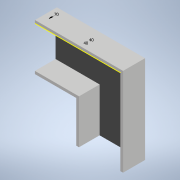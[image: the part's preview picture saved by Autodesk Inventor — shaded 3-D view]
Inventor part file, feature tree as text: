
AUTODESK INVENTOR PART (.ipt)
format: ipt  version: 2022 (Build 260153000, 153)  size: 157,696 bytes
history: native  units: mm
features: sketch x3, extrude x2, projected_geometry x2, other x1
ambient origin geometry x8: Origin, YZ Plane, XZ Plane, XY Plane, X Axis, Y Axis, Z Axis, Center Point
bodies: Body1 (feature_tree)
feature tree (8):
  other  "Твердое тело1"
  extrude  "Выдавливание1"  Depth=300.0mm
  extrude  "Выдавливание2"  Depth=300.0mm
  sketch  "Эскиз3"
  sketch  "Эскиз1"
  sketch  "Эскиз2"
  projected_geometry  "Спроецированная петля1"
  projected_geometry  "Спроецированная петля2"
